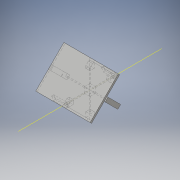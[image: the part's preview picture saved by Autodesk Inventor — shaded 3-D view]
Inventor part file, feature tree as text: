
AUTODESK INVENTOR PART (.ipt)
format: ipt  version: 2016 (Build 200138000, 138)  size: 280,064 bytes
history: native  units: mm
features: extrude x17, sketch x17, plane x5, mirror x3, other x1, projected_geometry x1
ambient origin geometry x8: Origin, YZ Plane, XZ Plane, XY Plane, X Axis, Y Axis, Z Axis, Center Point
bodies: 实体1 (feature_tree)
feature tree (44):
  extrude  "拉伸1"  Depth=200.0mm TaperAngle=0.0deg
  extrude  "拉伸3"  Depth=57.0mm TaperAngle=0.0deg
  extrude  "拉伸4"  Depth=10.0mm
  extrude  "拉伸5"  Depth=10.0mm
  extrude  "拉伸6"  Depth=200.0mm TaperAngle=0.0deg
  extrude  "拉伸7"  [1 undecoded]
  extrude  "拉伸8"  Depth=40.0mm
  plane  "工作平面4"
  extrude  "拉伸12"  Depth=20.0mm
  extrude  "拉伸17"  Depth=180.0mm TaperAngle=0.0deg
  extrude  "拉伸18"  Depth=42.0mm
  mirror  "镜像1"
  extrude  "拉伸19"  Depth=10.0mm TaperAngle=0.0deg
  plane  "工作平面6"
  mirror  "镜像2"
  plane  "工作平面7"
  mirror  "镜像3"
  extrude  "拉伸20"  Depth=40.0mm
  other  "工作轴1"
  extrude  "拉伸22"  Depth=350.0mm TaperAngle=0.0deg
  extrude  "拉伸23"  Depth=10.0mm TaperAngle=0.0deg
  extrude  "拉伸24"  Depth=15.0mm TaperAngle=0.0deg
  extrude  "拉伸25"  Depth=15.0mm TaperAngle=0.0deg
  extrude  "拉伸26"  [1 undecoded]
  sketch  "草图1"  dims[d1=10.0mm d2=200.0mm d3=0.0mm]
  sketch  "草图2"  dims[d4=57.0mm d7=57.0mm d8=0.0mm]
  sketch  "草图3"  dims[d9=200.0mm d10=0.0mm d11=10.0mm]
  sketch  "草图4"  dims[d12=200.0mm d13=0.0mm d14=10.0mm]
  sketch  "草图5"  dims[d15=200.0mm d16=0.0mm d17=200.0mm d18=0.0mm]
  sketch  "草图6"  dims[d19=200.0mm d20=0.0mm d30=-165.0mm]
  sketch  "草图7"  dims[d31=20.0mm d32=0.0mm d50=40.0mm]
  plane  "工作平面3"
  sketch  "草图11"  dims[d51=20.0mm d52=20.0mm]
  projected_geometry  "投影回路2"
  sketch  "草图17"  dims[d53=40.0mm d54=180.0mm d55=0.0mm]
  sketch  "草图18"  dims[d56=180.0mm d57=0.0mm d58=42.0mm]
  plane  "工作平面5"
  sketch  "草图19"  dims[d59=42.0mm d60=10.0mm d61=40.0mm d62=0.0mm d63=0.0mm]
  sketch  "草图20"  dims[d64=350.0mm d65=0.0mm d66=40.0mm]
  sketch  "草图21"  dims[d67=18.0mm d70=350.0mm d71=0.0mm]
  sketch  "草图22"  dims[d72=20.0mm d73=10.0mm d74=0.0mm]
  sketch  "草图23"  dims[d75=15.0mm d76=15.0mm d77=0.0mm]
  sketch  "草图24"  dims[d78=10.0mm d79=0.0mm d80=15.0mm d81=0.0mm]
  sketch  "草图25"
note: 2 required parameter values undecoded (feature->parameter linkage not recoverable at this tier; creation-order binding heuristic only, values carry confidence <= 0.55)
